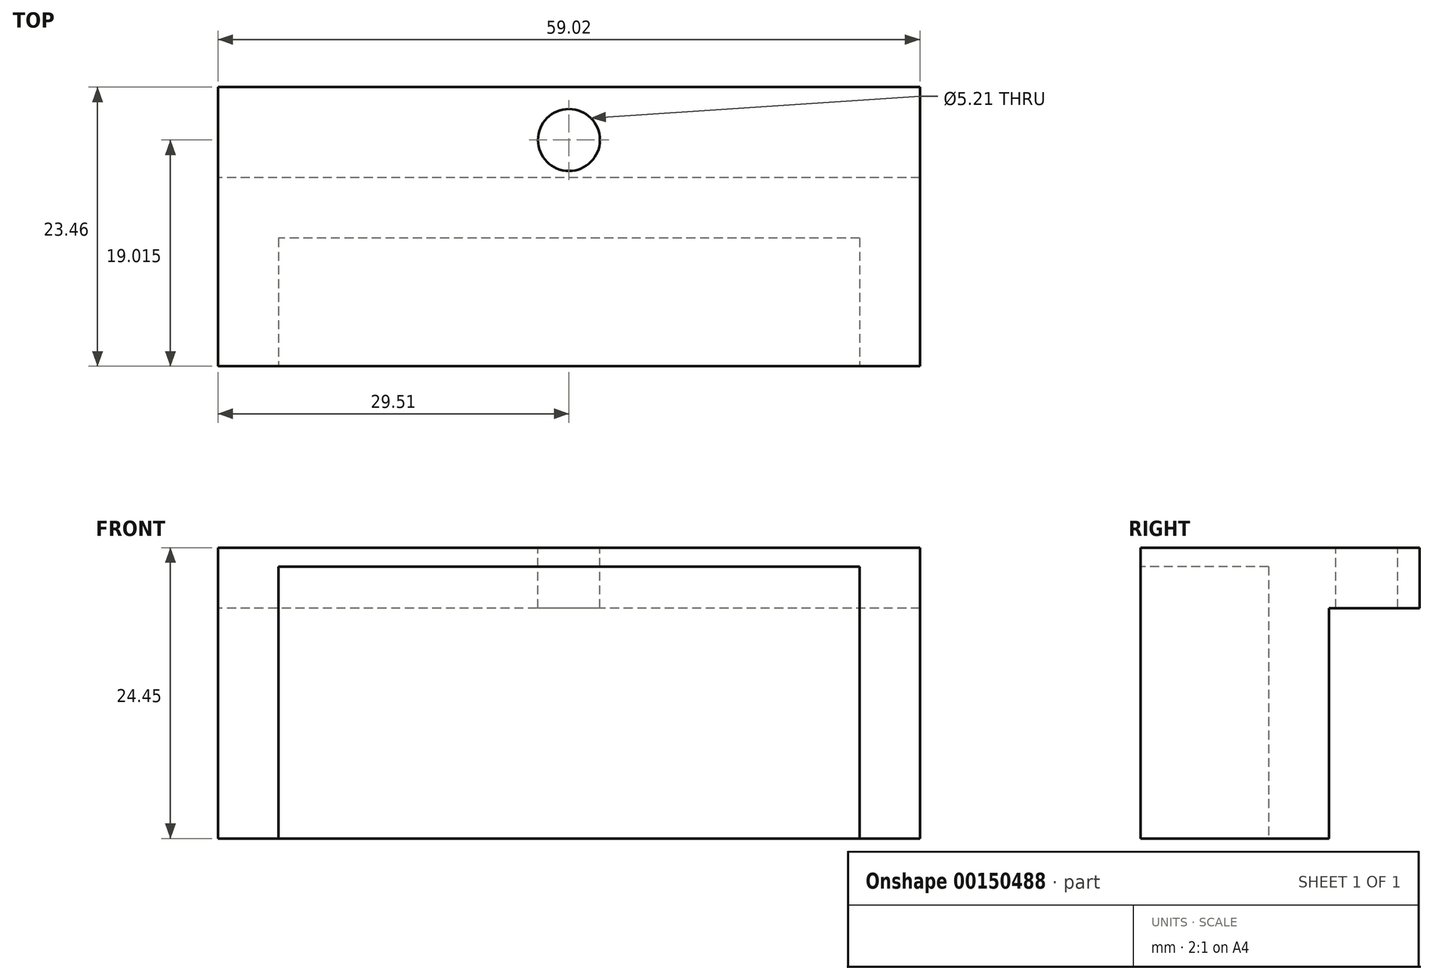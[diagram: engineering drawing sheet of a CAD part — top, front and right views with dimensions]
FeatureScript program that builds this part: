
annotation { "Feature Type Name" : "Feature", "Feature Type Description" : "" }
export const myFeature = defineFeature(function(context is Context, id is Id, definition is map)
    precondition{}
    {
        {
            var Q0;
            Q0=qCreatedBy(makeId("Top.planeOp"),FACE);
            var sketch = newSketch(context, id + "F0", { "sketchPlane" : qUnion([Q0])});
            skLineSegment(sketch, "E0.bottom", {"start": v(24.43, 5.38) * mm, "end": v(-24.43, 5.38) * mm});
            skLineSegment(sketch, "E0.top", {"start": v(24.43, -5.38) * mm, "end": v(-24.43, -5.38) * mm});
            skLineSegment(sketch, "E0.left", {"start": v(24.43, 5.38) * mm, "end": v(24.43, -5.38) * mm});
            skLineSegment(sketch, "E0.right", {"start": v(-24.43, 5.38) * mm, "end": v(-24.43, -5.38) * mm});
            skPoint(sketch, "E0.middle", {"position": v(0, 0) * mm});
            skLineSegment(sketch, "E1.bottom", {"start": v(29.51, 10.46) * mm, "end": v(-29.51, 10.46) * mm});
            skLineSegment(sketch, "E1.top", {"start": v(29.51, -10.46) * mm, "end": v(-29.51, -10.46) * mm});
            skLineSegment(sketch, "E1.left", {"start": v(29.51, 10.46) * mm, "end": v(29.51, -10.46) * mm});
            skLineSegment(sketch, "E1.right", {"start": v(-29.51, 10.46) * mm, "end": v(-29.51, -10.46) * mm});
            skSolve(sketch);
        }
        {
            var Q0;
            Q0=makeQuery(id+"F0.imprint","IMPRINT",FACE,{"disambiguationData":[TD([[makeQuery(id+"F0.imprint","IMPRINT",EDGE,{"derivedFrom":sQuery(id+"F0.wireOp",EDGE,"E0.bottom")}),-1.0]])]});
            extrude(context, id + "F1", {"entities" : qUnion([Q0]), "depth" : 24.45 * mm});
        }
        {
            var Q0;
            Q0=makeQuery(id+"F1.opExtrude","CAP_FACE",FACE,{"disambiguationData":[OSD([sQuery(id+"F0.wireOp",EDGE,"E0.bottom"),sQuery(id+"F0.wireOp",EDGE,"E0.top"),sQuery(id+"F0.wireOp",EDGE,"E0.left"),sQuery(id+"F0.wireOp",EDGE,"E0.right"),sQuery(id+"F0.wireOp",EDGE,"E1.bottom"),sQuery(id+"F0.wireOp",EDGE,"E1.top"),sQuery(id+"F0.wireOp",EDGE,"E1.left"),sQuery(id+"F0.wireOp",EDGE,"E1.right")])],"isStart":false});
            var sketch = newSketch(context, id + "F2", { "sketchPlane" : qUnion([Q0])});
            skLineSegment(sketch, "E2.bottom", {"start": v(-29.51, 10.46) * mm, "end": v(29.51, 10.46) * mm});
            skLineSegment(sketch, "E2.top", {"start": v(-29.51, 18.08) * mm, "end": v(29.51, 18.08) * mm});
            skLineSegment(sketch, "E2.left", {"start": v(-29.51, 10.46) * mm, "end": v(-29.51, 18.08) * mm});
            skLineSegment(sketch, "E2.right", {"start": v(29.51, 10.46) * mm, "end": v(29.51, 18.08) * mm});
            skCircle(sketch, "E3", {"center": v(0, 13.64) * mm, "radius": 2.6 * mm});
            skPoint(sketch, "E3.centerSnap0", {"position": v(0, 10.46) * mm});
            skLineSegment(sketch, "E4", {"start": v(-29.51, 14.27) * mm, "end": v(29.51, 14.27) * mm, "construction": true});
            skSolve(sketch);
        }
        {
            var Q0;
            Q0=makeQuery(id+"F2.imprint","IMPRINT",FACE,{"disambiguationData":[TD([[makeQuery(id+"F2.imprint","IMPRINT",EDGE,{"derivedFrom":sQuery(id+"F2.wireOp",EDGE,"E2.bottom")}),-1.0]])]});
            extrude(context, id + "F3", {"entities" : qUnion([Q0]), "operationType" : NewBodyOperationType.ADD, "oppositeDirection" : true, "depth" : 5.08 * mm});
        }
        {
            var Q0;
            Q0=makeQuery(id+"F1.opExtrude","CAP_FACE",FACE,{"disambiguationData":[OSD([sQuery(id+"F0.wireOp",EDGE,"E0.bottom"),sQuery(id+"F0.wireOp",EDGE,"E0.top"),sQuery(id+"F0.wireOp",EDGE,"E0.left"),sQuery(id+"F0.wireOp",EDGE,"E0.right"),sQuery(id+"F0.wireOp",EDGE,"E1.bottom"),sQuery(id+"F0.wireOp",EDGE,"E1.top"),sQuery(id+"F0.wireOp",EDGE,"E1.left"),sQuery(id+"F0.wireOp",EDGE,"E1.right")])],"isStart":true});
            var sketch = newSketch(context, id + "F4", { "sketchPlane" : qUnion([Q0])});
            skLineSegment(sketch, "E5.bottom", {"start": v(29.51, 5.38) * mm, "end": v(-29.51, 5.38) * mm});
            skLineSegment(sketch, "E5.top", {"start": v(29.51, 10.46) * mm, "end": v(-29.51, 10.46) * mm});
            skLineSegment(sketch, "E5.left", {"start": v(29.51, 5.38) * mm, "end": v(29.51, 10.46) * mm});
            skLineSegment(sketch, "E5.right", {"start": v(-29.51, 5.38) * mm, "end": v(-29.51, 10.46) * mm});
            skSolve(sketch);
        }
        {
            var Q0;
            Q0=makeQuery(id+"F4.imprint","IMPRINT",FACE,{"disambiguationData":[TD([[makeQuery(id+"F4.imprint","IMPRINT",EDGE,{"derivedFrom":sQuery(id+"F4.wireOp",EDGE,"E5.bottom")}),-1.0]])]});
            extrude(context, id + "F5", {"entities" : qUnion([Q0]), "operationType" : NewBodyOperationType.REMOVE, "endBound" : BoundingType.THROUGH_ALL, "oppositeDirection" : true, "depth" : 25.4 * mm});
        }
        {
            var Q0;
            Q0=makeQuery(id+"F3.boolean.opBoolean","MERGE",FACE,{"derivedFrom":[makeQuery(id+"F1.opExtrude","CAP_FACE",FACE,{"disambiguationData":[OSD([sQuery(id+"F0.wireOp",EDGE,"E0.bottom"),sQuery(id+"F0.wireOp",EDGE,"E0.top"),sQuery(id+"F0.wireOp",EDGE,"E0.left"),sQuery(id+"F0.wireOp",EDGE,"E0.right"),sQuery(id+"F0.wireOp",EDGE,"E1.bottom"),sQuery(id+"F0.wireOp",EDGE,"E1.top"),sQuery(id+"F0.wireOp",EDGE,"E1.left"),sQuery(id+"F0.wireOp",EDGE,"E1.right")])],"isStart":false}),makeQuery(id+"F3.opExtrude","CAP_FACE",FACE,{"disambiguationData":[OSD([sQuery(id+"F2.wireOp",EDGE,"E2.bottom"),sQuery(id+"F2.wireOp",EDGE,"E2.top"),sQuery(id+"F2.wireOp",EDGE,"E2.left"),sQuery(id+"F2.wireOp",EDGE,"E2.right"),sQuery(id+"F2.wireOp",EDGE,"E3")])],"isStart":true})]});
            var sketch = newSketch(context, id + "F6", { "sketchPlane" : qUnion([Q0])});
            skLineSegment(sketch, "E6.bottom", {"start": v(24.43, 5.38) * mm, "end": v(-24.43, 5.38) * mm});
            skLineSegment(sketch, "E6.top", {"start": v(24.43, -5.38) * mm, "end": v(-24.43, -5.38) * mm});
            skLineSegment(sketch, "E6.left", {"start": v(24.43, 5.38) * mm, "end": v(24.43, -5.38) * mm});
            skLineSegment(sketch, "E6.right", {"start": v(-24.43, 5.38) * mm, "end": v(-24.43, -5.38) * mm});
            skSolve(sketch);
        }
        {
            var Q0;
            Q0=makeQuery(id+"F6.imprint","IMPRINT",FACE,{"disambiguationData":[TD([[makeQuery(id+"F6.imprint","IMPRINT",EDGE,{"derivedFrom":sQuery(id+"F6.wireOp",EDGE,"E6.bottom")}),1.0]])]});
            extrude(context, id + "F7", {"entities" : qUnion([Q0]), "operationType" : NewBodyOperationType.ADD, "oppositeDirection" : true, "depth" : 1.59 * mm});
        }
    });
